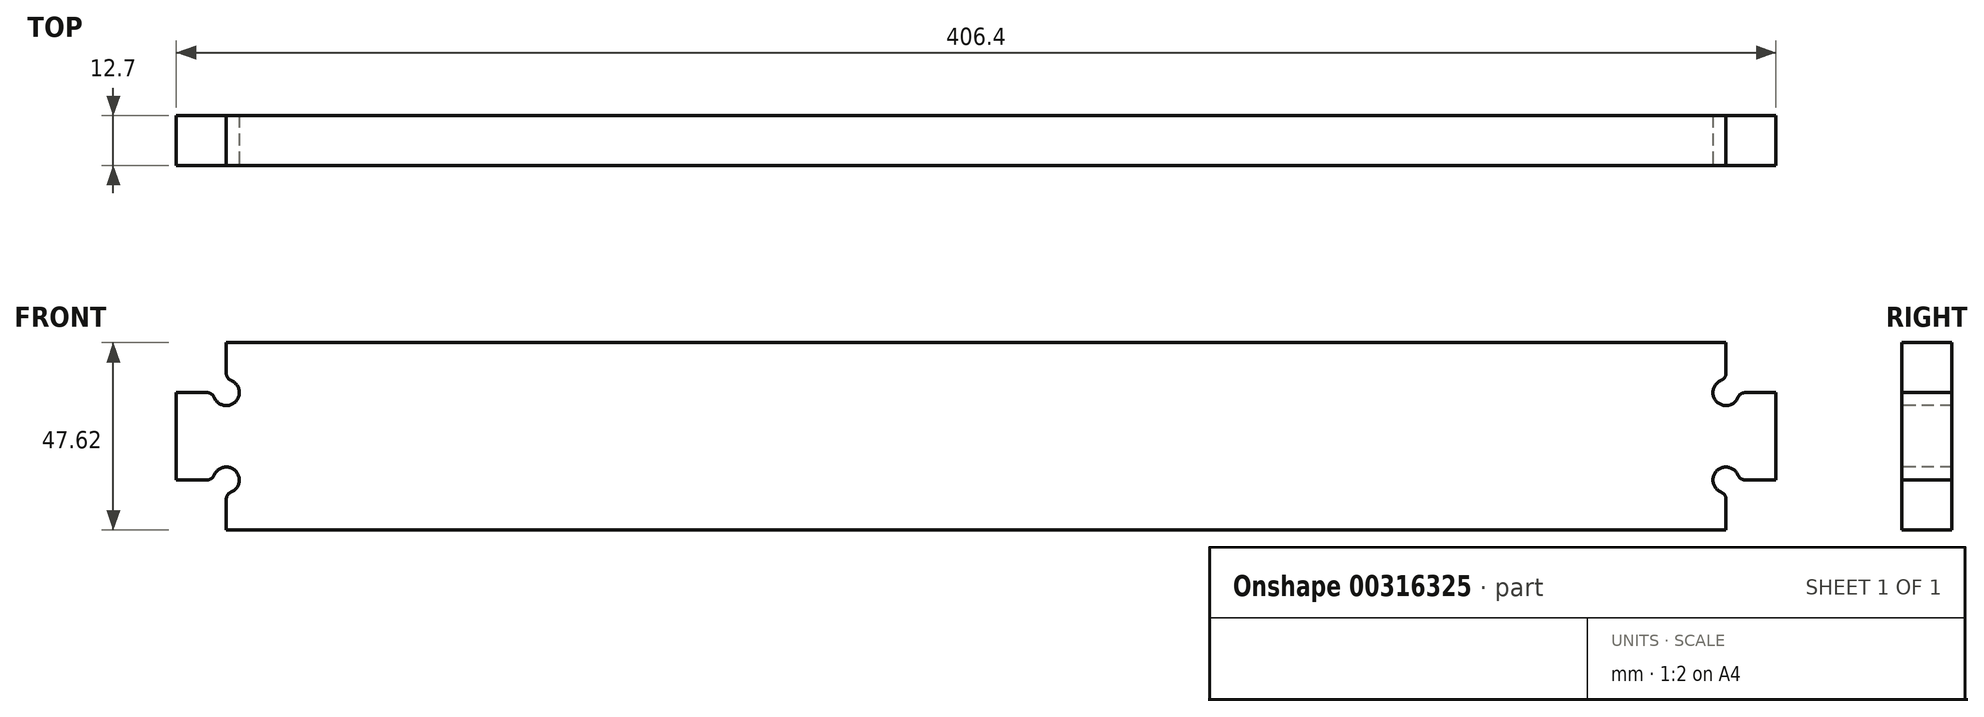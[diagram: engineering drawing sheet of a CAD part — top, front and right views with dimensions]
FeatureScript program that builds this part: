
annotation { "Feature Type Name" : "Feature", "Feature Type Description" : "" }
export const myFeature = defineFeature(function(context is Context, id is Id, definition is map)
    precondition{}
    {
        {
            var Q0;
            Q0=qCreatedBy(makeId("Front.planeOp"),FACE);
            var sketch = newSketch(context, id + "F0", { "sketchPlane" : qUnion([Q0])});
            skLineSegment(sketch, "E0.bottom", {"start": v(0, 0) * mm, "end": v(406.4, 0) * mm});
            skLineSegment(sketch, "E0.top", {"start": v(0, 47.63) * mm, "end": v(406.4, 47.63) * mm});
            skLineSegment(sketch, "E0.left", {"start": v(0, 0) * mm, "end": v(0, 47.63) * mm});
            skLineSegment(sketch, "E0.right", {"start": v(406.4, 0) * mm, "end": v(406.4, 47.63) * mm});
            skSolve(sketch);
        }
        {
            var Q0;
            Q0 = qSketchRegion(id + "F0", true);
            extrude(context, id + "F1", {"entities" : qUnion([Q0]), "depth" : 12.7 * mm});
        }
        {
            var Q0;
            Q0=makeQuery(id+"F1.opExtrude","CAP_FACE",FACE,{"disambiguationData":[OSD([sQuery(id+"F0.wireOp",EDGE,"E0.bottom"),sQuery(id+"F0.wireOp",EDGE,"E0.top"),sQuery(id+"F0.wireOp",EDGE,"E0.left"),sQuery(id+"F0.wireOp",EDGE,"E0.right")])],"isStart":false});
            var sketch = newSketch(context, id + "F2", { "sketchPlane" : qUnion([Q0])});
            skLineSegment(sketch, "E1.bottom", {"start": v(0, 47.63) * mm, "end": v(12.7, 47.63) * mm});
            skLineSegment(sketch, "E1.top", {"start": v(0, 34.93) * mm, "end": v(7.77, 34.93) * mm});
            skLineSegment(sketch, "E1.left", {"start": v(0, 47.63) * mm, "end": v(0, 34.93) * mm});
            skLineSegment(sketch, "E1.right", {"start": v(12.7, 47.63) * mm, "end": v(12.7, 39.86) * mm});
            skLineSegment(sketch, "E2.bottom", {"start": v(0, 0) * mm, "end": v(12.7, 0) * mm});
            skLineSegment(sketch, "E2.top", {"start": v(0, 12.7) * mm, "end": v(7.77, 12.7) * mm});
            skLineSegment(sketch, "E2.left", {"start": v(0, 0) * mm, "end": v(0, 12.7) * mm});
            skLineSegment(sketch, "E2.right", {"start": v(12.7, 0) * mm, "end": v(12.7, 7.77) * mm});
            skArc(sketch, "E3", {"start": v(9.65, 33.67) * mm, "mid": v(15.03, 32.6) * mm, "end": v(13.96, 37.98) * mm});
            skArc(sketch, "E4", {"start": v(13.96, 9.65) * mm, "mid": v(15.03, 15.03) * mm, "end": v(9.65, 13.96) * mm});
            skPoint(sketch, "E5.visualSharp", {"position": v(9.4, 34.93) * mm});
            skArc(sketch, "E5.filletArc", {"start": v(9.65, 33.67) * mm, "mid": v(8.9, 34.58) * mm, "end": v(7.77, 34.92) * mm});
            skPoint(sketch, "E6.visualSharp", {"position": v(12.7, 38.23) * mm});
            skArc(sketch, "E6.filletArc", {"start": v(12.7, 39.86) * mm, "mid": v(13.04, 38.73) * mm, "end": v(13.96, 37.98) * mm});
            skPoint(sketch, "E7.visualSharp", {"position": v(9.4, 12.7) * mm});
            skArc(sketch, "E7.filletArc", {"start": v(7.77, 12.7) * mm, "mid": v(8.9, 13.04) * mm, "end": v(9.65, 13.96) * mm});
            skPoint(sketch, "E8.visualSharp", {"position": v(12.7, 9.4) * mm});
            skArc(sketch, "E8.filletArc", {"start": v(13.96, 9.65) * mm, "mid": v(13.04, 8.9) * mm, "end": v(12.7, 7.77) * mm});
            skLineSegment(sketch, "E9", {"start": v(203.2, 47.63) * mm, "end": v(203.2, -46.5) * mm, "construction": true});
            skArc(sketch, "E10.MirrorCS", {"start": v(398.63, 12.7) * mm, "mid": v(397.5, 13.04) * mm, "end": v(396.75, 13.96) * mm});
            skArc(sketch, "E11.MirrorCS", {"start": v(396.75, 33.67) * mm, "mid": v(397.5, 34.58) * mm, "end": v(398.63, 34.92) * mm});
            skArc(sketch, "E12.MirrorCS", {"start": v(393.7, 39.86) * mm, "mid": v(393.36, 38.73) * mm, "end": v(392.44, 37.98) * mm});
            skArc(sketch, "E13.MirrorCS", {"start": v(392.44, 9.65) * mm, "mid": v(393.36, 8.9) * mm, "end": v(393.7, 7.77) * mm});
            skLineSegment(sketch, "E14.MirrorCS", {"start": v(406.4, 34.93) * mm, "end": v(398.63, 34.93) * mm});
            skLineSegment(sketch, "E15.MirrorCS", {"start": v(406.4, 12.7) * mm, "end": v(398.63, 12.7) * mm});
            skLineSegment(sketch, "E16.MirrorCS", {"start": v(393.7, 0) * mm, "end": v(393.7, 7.77) * mm});
            skArc(sketch, "E17.MirrorCS", {"start": v(396.75, 33.67) * mm, "mid": v(391.37, 32.6) * mm, "end": v(392.44, 37.98) * mm});
            skLineSegment(sketch, "E18.MirrorCS", {"start": v(393.7, 47.63) * mm, "end": v(393.7, 39.86) * mm});
            skArc(sketch, "E19.MirrorCS", {"start": v(392.44, 9.65) * mm, "mid": v(391.37, 15.03) * mm, "end": v(396.75, 13.96) * mm});
            skPoint(sketch, "E20.MirrorP", {"position": v(397, 12.7) * mm});
            skPoint(sketch, "E21.MirrorP", {"position": v(397, 34.93) * mm});
            skLineSegment(sketch, "E22.MirrorCS", {"start": v(406.4, 47.63) * mm, "end": v(406.4, 34.93) * mm});
            skLineSegment(sketch, "E23.MirrorCS", {"start": v(406.4, 0) * mm, "end": v(406.4, 12.7) * mm});
            skPoint(sketch, "E24.MirrorP", {"position": v(393.7, 9.4) * mm});
            skLineSegment(sketch, "E25.MirrorCS", {"start": v(406.4, 0) * mm, "end": v(393.7, 0) * mm});
            skLineSegment(sketch, "E26.MirrorCS", {"start": v(406.4, 47.63) * mm, "end": v(393.7, 47.63) * mm});
            skPoint(sketch, "E27.MirrorP", {"position": v(393.7, 38.23) * mm});
            skSolve(sketch);
        }
        {
            var Q0;
            Q0 = qSketchRegion(id + "F2", true);
            extrude(context, id + "F3", {"entities" : qUnion([Q0]), "operationType" : NewBodyOperationType.REMOVE, "oppositeDirection" : true, "depth" : 25.4 * mm});
        }
    });
